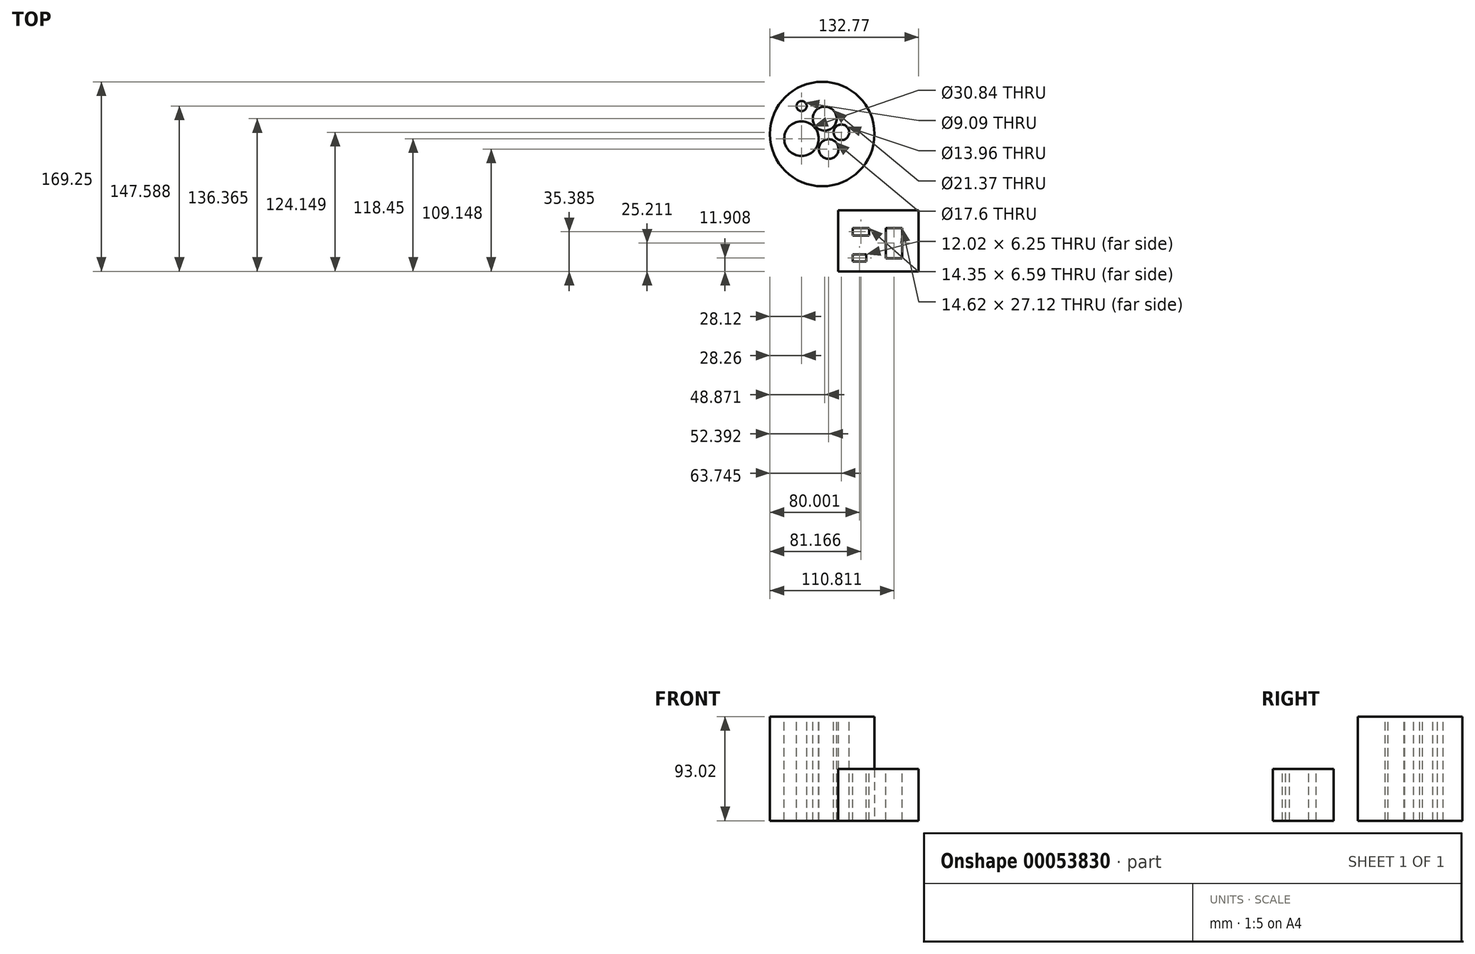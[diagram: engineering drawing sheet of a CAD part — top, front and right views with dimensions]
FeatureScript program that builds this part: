
annotation { "Feature Type Name" : "Feature", "Feature Type Description" : "" }
export const myFeature = defineFeature(function(context is Context, id is Id, definition is map)
    precondition{}
    {
        {
            var Q0;
            Q0=qCreatedBy(makeId("Top.planeOp"),FACE);
            var sketch = newSketch(context, id + "F0", { "sketchPlane" : qUnion([Q0])});
            skCircle(sketch, "E0", {"center": v(-27.34, 56.16) * mm, "radius": 46.66 * mm});
            skSolve(sketch);
        }
        {
            var Q0;
            Q0=makeQuery(id+"F0.imprint","IMPRINT",FACE,{"disambiguationData":[TD([[makeQuery(id+"F0.imprint","IMPRINT",EDGE,{"derivedFrom":sQuery(id+"F0.wireOp",EDGE,"E0")}),1.0]])]});
            extrude(context, id + "F1", {"entities" : qUnion([Q0]), "depth" : 93.02 * mm});
        }
        {
            var Q0;
            Q0=makeQuery(id+"F1.opExtrude","CAP_FACE",FACE,{"disambiguationData":[OSD([sQuery(id+"F0.wireOp",EDGE,"E0")])],"isStart":false});
            var sketch = newSketch(context, id + "F2", { "sketchPlane" : qUnion([Q0])});
            skCircle(sketch, "E1", {"center": v(-45.87, 52.01) * mm, "radius": 15.42 * mm});
            skCircle(sketch, "E2", {"center": v(-21.6, 42.7) * mm, "radius": 8.8 * mm});
            skCircle(sketch, "E3", {"center": v(-25.12, 69.92) * mm, "radius": 10.69 * mm});
            skCircle(sketch, "E4", {"center": v(-10.25, 57.7) * mm, "radius": 6.98 * mm});
            skCircle(sketch, "E5", {"center": v(-45.73, 81.15) * mm, "radius": 4.55 * mm});
            skSolve(sketch);
        }
        {
            var Q0;
            Q0 = qSketchRegion(id + "F2", true);
            extrude(context, id + "F3", {"entities" : qUnion([Q0]), "operationType" : NewBodyOperationType.REMOVE, "endBound" : BoundingType.THROUGH_ALL, "oppositeDirection" : true, "depth" : 25.4 * mm});
        }
        {
            var Q0;
            Q0=qCreatedBy(makeId("Top.planeOp"),FACE);
            var sketch = newSketch(context, id + "F4", { "sketchPlane" : qUnion([Q0])});
            skLineSegment(sketch, "E6.bottom", {"start": v(58.78, -11.94) * mm, "end": v(-13.22, -11.94) * mm});
            skLineSegment(sketch, "E6.top", {"start": v(58.78, -66.44) * mm, "end": v(-13.22, -66.44) * mm});
            skLineSegment(sketch, "E6.left", {"start": v(58.78, -11.94) * mm, "end": v(58.78, -66.44) * mm});
            skLineSegment(sketch, "E6.right", {"start": v(-13.22, -11.94) * mm, "end": v(-13.22, -66.44) * mm});
            skSolve(sketch);
        }
        {
            var Q0;
            Q0 = qSketchRegion(id + "F4", true);
            extrude(context, id + "F5", {"entities" : qUnion([Q0]), "depth" : 46.13 * mm});
        }
        {
            var Q0;
            Q0=makeQuery(id+"F5.opExtrude","CAP_FACE",FACE,{"disambiguationData":[OSD([sQuery(id+"F4.wireOp",EDGE,"E6.bottom"),sQuery(id+"F4.wireOp",EDGE,"E6.top"),sQuery(id+"F4.wireOp",EDGE,"E6.left"),sQuery(id+"F4.wireOp",EDGE,"E6.right")])],"isStart":false});
            var sketch = newSketch(context, id + "F6", { "sketchPlane" : qUnion([Q0])});
            skLineSegment(sketch, "E7.bottom", {"start": v(0, -57.66) * mm, "end": v(12.02, -57.66) * mm});
            skLineSegment(sketch, "E7.top", {"start": v(0, -51.4) * mm, "end": v(12.02, -51.4) * mm});
            skLineSegment(sketch, "E7.left", {"start": v(0, -57.66) * mm, "end": v(0, -51.4) * mm});
            skLineSegment(sketch, "E7.right", {"start": v(12.02, -57.66) * mm, "end": v(12.02, -51.4) * mm});
            skLineSegment(sketch, "E8.bottom", {"start": v(0, -34.35) * mm, "end": v(14.35, -34.35) * mm});
            skLineSegment(sketch, "E8.top", {"start": v(0, -27.76) * mm, "end": v(14.35, -27.76) * mm});
            skLineSegment(sketch, "E8.left", {"start": v(0, -34.35) * mm, "end": v(0, -27.76) * mm});
            skLineSegment(sketch, "E8.right", {"start": v(14.35, -34.35) * mm, "end": v(14.35, -27.76) * mm});
            skLineSegment(sketch, "E9.bottom", {"start": v(29.51, -54.79) * mm, "end": v(44.13, -54.79) * mm});
            skLineSegment(sketch, "E9.top", {"start": v(29.51, -27.67) * mm, "end": v(44.13, -27.67) * mm});
            skLineSegment(sketch, "E9.left", {"start": v(29.51, -54.79) * mm, "end": v(29.51, -27.67) * mm});
            skLineSegment(sketch, "E9.right", {"start": v(44.13, -54.79) * mm, "end": v(44.13, -27.67) * mm});
            skPoint(sketch, "E10.oppositeSnap0", {"position": v(29.51, -41.23) * mm});
            skLineSegment(sketch, "E10.bottom", {"start": v(29.51, -47.77) * mm, "end": v(37.41, -47.77) * mm});
            skLineSegment(sketch, "E10.top", {"start": v(29.51, -41.23) * mm, "end": v(37.41, -41.23) * mm});
            skLineSegment(sketch, "E10.left", {"start": v(29.51, -47.77) * mm, "end": v(29.51, -41.23) * mm});
            skLineSegment(sketch, "E10.right", {"start": v(37.41, -47.77) * mm, "end": v(37.41, -41.23) * mm});
            skLineSegment(sketch, "E11.bottom", {"start": v(44.13, -36.31) * mm, "end": v(36.82, -36.31) * mm});
            skLineSegment(sketch, "E11.top", {"start": v(44.13, -27.67) * mm, "end": v(36.82, -27.67) * mm});
            skLineSegment(sketch, "E11.left", {"start": v(44.13, -36.31) * mm, "end": v(44.13, -27.67) * mm});
            skLineSegment(sketch, "E11.right", {"start": v(36.82, -36.31) * mm, "end": v(36.82, -27.67) * mm});
            skSolve(sketch);
        }
        {
            var Q0;
            Q0=makeQuery(id+"F6.imprint","IMPRINT",FACE,{"disambiguationData":[TD([[makeQuery(id+"F6.imprint","IMPRINT",EDGE,{"derivedFrom":sQuery(id+"F6.wireOp",EDGE,"E7.bottom")}),1.0]])]});
            var Q1;
            Q1=makeQuery(id+"F6.imprint","IMPRINT",FACE,{"disambiguationData":[TD([[makeQuery(id+"F6.imprint","IMPRINT",EDGE,{"derivedFrom":sQuery(id+"F6.wireOp",EDGE,"E8.bottom")}),1.0]])]});
            var Q2;
            Q2=makeQuery(id+"F6.imprint","IMPRINT",FACE,{"disambiguationData":[TD([[makeQuery(id+"F6.imprint","IMPRINT",EDGE,{"derivedFrom":sQuery(id+"F6.wireOp",EDGE,"E10.bottom")}),1.0]])]});
            var Q3;
            Q3=makeQuery(id+"F6.imprint","IMPRINT",FACE,{"disambiguationData":[TD([[makeQuery(id+"F6.imprint","IMPRINT",EDGE,{"derivedFrom":sQuery(id+"F6.wireOp",EDGE,"E11.bottom")}),-1.0]])]});
            var Q4;
            {var subQ4=sQuery(id+"F6.wireOp",EDGE,"E9.bottom");Q4=makeQuery(id+"F6.imprint","IMPRINT",FACE,{"disambiguationData":[TD([[makeQuery(id+"F6.imprint","IMPRINT",EDGE,{"derivedFrom":subQ4}),1.0]])]});}
            extrude(context, id + "F7", {"entities" : qUnion([Q0, Q1, Q2, Q3, Q4]), "operationType" : NewBodyOperationType.REMOVE, "endBound" : BoundingType.THROUGH_ALL, "oppositeDirection" : true, "depth" : 25.4 * mm});
        }
    });
